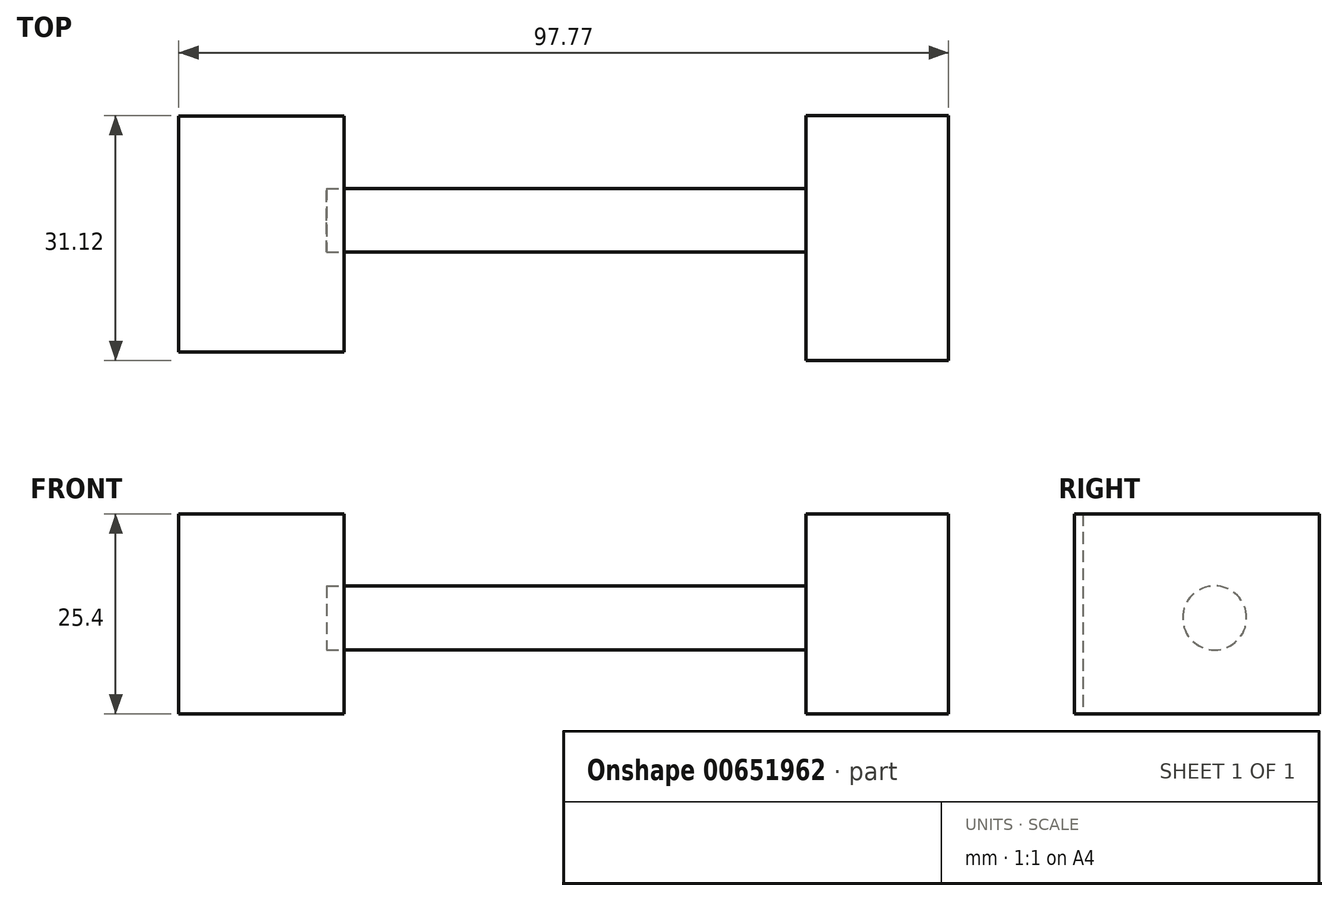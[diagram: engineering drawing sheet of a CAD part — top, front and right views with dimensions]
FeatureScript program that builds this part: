
annotation { "Feature Type Name" : "Feature", "Feature Type Description" : "" }
export const myFeature = defineFeature(function(context is Context, id is Id, definition is map)
    precondition{}
    {
        {
            var Q0;
            Q0=qCreatedBy(makeId("Top.planeOp"),FACE);
            var sketch = newSketch(context, id + "F0", { "sketchPlane" : qUnion([Q0])});
            skLineSegment(sketch, "E0.bottom", {"start": v(26.06, 13.31) * mm, "end": v(44.16, 13.31) * mm});
            skLineSegment(sketch, "E0.top", {"start": v(26.06, -17.8) * mm, "end": v(44.16, -17.8) * mm});
            skLineSegment(sketch, "E0.left", {"start": v(26.06, 13.31) * mm, "end": v(26.06, -17.8) * mm});
            skLineSegment(sketch, "E0.right", {"start": v(44.16, 13.31) * mm, "end": v(44.16, -17.8) * mm});
            skSolve(sketch);
        }
        {
            var Q0;
            Q0 = qSketchRegion(id + "F0", true);
            extrude(context, id + "F1", {"entities" : qUnion([Q0]), "depth" : 25.4 * mm, "offsetDistance" : 25.4 * mm});
        }
        {
            var Q0;
            Q0=qCreatedBy(makeId("Top.planeOp"),FACE);
            var sketch = newSketch(context, id + "F2", { "sketchPlane" : qUnion([Q0])});
            skLineSegment(sketch, "E1.bottom", {"start": v(-53.6, 13.22) * mm, "end": v(-32.6, 13.22) * mm});
            skLineSegment(sketch, "E1.top", {"start": v(-53.6, -16.74) * mm, "end": v(-32.6, -16.74) * mm});
            skLineSegment(sketch, "E1.left", {"start": v(-53.6, 13.22) * mm, "end": v(-53.6, -16.74) * mm});
            skLineSegment(sketch, "E1.right", {"start": v(-32.6, 13.22) * mm, "end": v(-32.6, -16.74) * mm});
            skSolve(sketch);
        }
        {
            var Q0;
            Q0 = qSketchRegion(id + "F2", true);
            extrude(context, id + "F3", {"entities" : qUnion([Q0]), "depth" : 25.4 * mm, "offsetDistance" : 25.4 * mm});
        }
        {
            var Q0;
            Q0=makeQuery(id+"F1.opExtrude","SWEPT_FACE",FACE,{"disambiguationData":[OSD([sQuery(id+"F0.wireOp",EDGE,"E0.left")])]});
            var sketch = newSketch(context, id + "F4", { "sketchPlane" : qUnion([Q0])});
            skCircle(sketch, "E2", {"center": v(0, 12.2) * mm, "radius": 4.06 * mm});
            skSolve(sketch);
        }
        {
            var Q0;
            Q0 = qSketchRegion(id + "F4", true);
            extrude(context, id + "F5", {"entities" : qUnion([Q0]), "depth" : 60.9 * mm, "offsetDistance" : 25.4 * mm});
        }
    });
